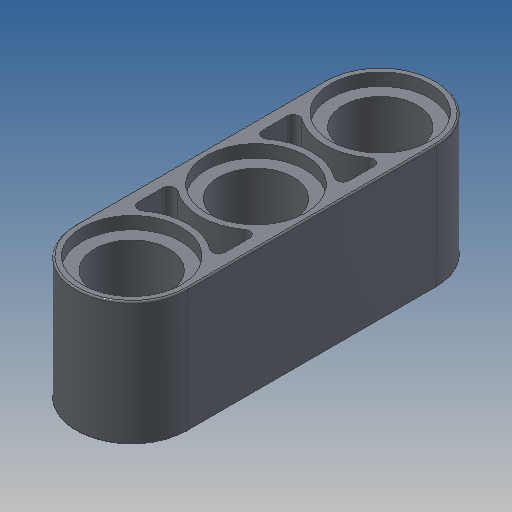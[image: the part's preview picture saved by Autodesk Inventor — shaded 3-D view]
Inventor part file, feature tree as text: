
AUTODESK INVENTOR PART (.ipt)
format: ipt  version: 2022.2 (Build 262287000, 287)  size: 237,568 bytes
history: native  units: mm
features: extrude x3, sketch x2, mirror x1, fillet x1
ambient origin geometry x8: Origin, YZ Plane, XZ Plane, XY Plane, X Axis, Y Axis, Z Axis, Center Point
bodies: Solid1 (feature_tree)
feature tree (7):
  extrude  "Extrusion1"  Depth=6.4mm
  sketch  "Sketch6"  dims[d14=8.0mm d15=0.0mm d32=7.2mm d34=8.0mm d36=0.8mm d41=0.8mm d42=0.0mm d43=3.1mm d44=0.0mm d45=0.1mm d46=0.4mm]
  extrude  "Extrusion7"  Depth=7.2mm
  extrude  "Extrusion8"  Depth=8.0mm
  mirror  "Mirror1"
  fillet  "Fillet1"  Radius=0.8mm
  sketch  "Sketch1"  dims[d8=4.8mm d9=6.4mm]
